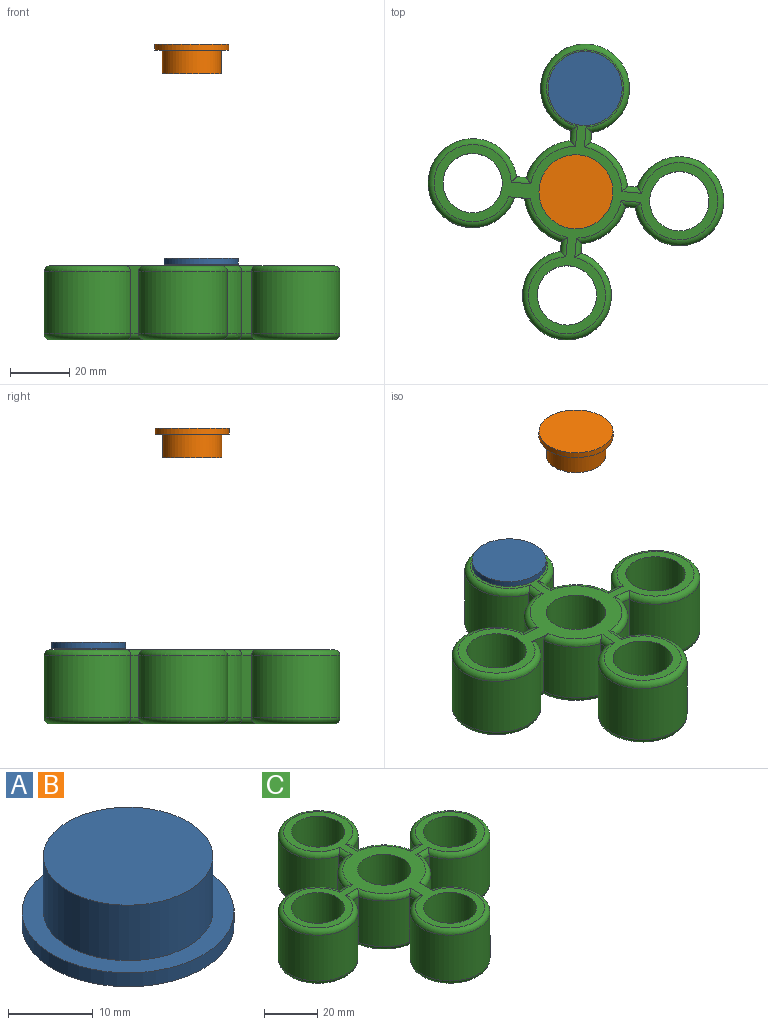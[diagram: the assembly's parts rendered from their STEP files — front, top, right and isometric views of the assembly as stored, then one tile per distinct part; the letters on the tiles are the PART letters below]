
ASSEMBLY  parts=3 mates=2
PART A: 5 faces, bbox 25x25x10 mm
  f0: cylinder r=10mm len=20mm, axis (0,0,-1), area 502.7mm2, adj f1,f3
  f1: plane 20x20mm, normal (0,0,1), area 314.2mm2, adj f0
  f2: cylinder r=12.5mm len=25mm, axis (0,0,-1), area 157.1mm2, adj f3,f4
  f3: plane 25x25mm, normal (0,0,1), area 176.7mm2, adj f0,f2
  f4: plane 25x25mm, normal (0,0,-1), area 490.9mm2, adj f2
PART B: same geometry as A
PART C: 54 faces, bbox 102.6x102.5x25 mm
  f0: plane 21x3.38mm, normal (0,-1,0), area 71.1mm2, adj f1,f19,f32,f38
  f1: cylinder r=17.5mm len=21mm, axis (0,0,-1), area 430mm2, adj f0,f2,f30,f39
  f2: plane 21x3.25mm, normal (-1,0,0), area 68.3mm2, adj f1,f3,f28,f41
  f3: cylinder r=15mm len=30mm, axis (0,0,-1), area 1830.8mm2, adj f2,f4,f26,f43
  f4: plane 23x7.4mm, normal (1,0,0), area 77.3mm2, adj f3,f5,f21,f23,f26,f45
  f5: cylinder r=17.5mm len=21mm, axis (0,0,-1), area 428.5mm2, adj f4,f6,f23,f47
  f6: plane 21x3.23mm, normal (0,-1,0), area 67.9mm2, adj f5,f7,f24,f49
  f7: cylinder r=15mm len=30mm, axis (0,0,-1), area 1830.8mm2, adj f6,f8,f25,f51
  f8: plane 21x3.23mm, normal (0,1,0), area 67.9mm2, adj f7,f9,f27,f53
  f9: cylinder r=17.5mm len=21mm, axis (0,0,-1), area 428.5mm2, adj f8,f10,f29,f52
  f10: plane 21x3.28mm, normal (1,0,0), area 68.9mm2, adj f9,f11,f31,f50
  f11: cylinder r=15mm len=30mm, axis (0,0,-1), area 1829.3mm2, adj f10,f12,f33,f48
  f12: plane 21x3.28mm, normal (-1,0,0), area 68.9mm2, adj f11,f13,f35,f46
  f13: cylinder r=17.5mm len=21mm, axis (0,0,-1), area 428.5mm2, adj f12,f14,f37,f44
  f14: plane 21x3.38mm, normal (0,1,0), area 71.1mm2, adj f13,f19,f36,f42
  f15: cylinder r=10mm len=25mm, axis (0,0,-1), area 1570.8mm2, adj f21,f22
  f16: cylinder r=10mm len=25mm, axis (0,0,-1), area 1570.8mm2, adj f21,f22
  f17: cylinder r=10mm len=25mm, axis (0,0,-1), area 1570.8mm2, adj f21,f22
  f18: cylinder r=10mm len=25mm, axis (0,0,-1), area 1570.8mm2, adj f21,f22
  f19: cylinder r=15mm len=30mm, axis (0,0,-1), area 1830.8mm2, adj f0,f14,f34,f40
  f20: cylinder r=10mm len=25mm, axis (0,0,-1), area 1570.8mm2, adj f21,f22
  f21: plane 96.08x96mm, normal (0,0,1), area 1401mm2, adj f4,f15,f16,f17,f18,f20,f23,f24
  f22: plane 96.08x96mm, normal (0,0,-1), area 1387mm2, adj f15,f16,f17,f18,f20,f38,f39,f40
  f23: torus R=15.5mm, axis (0,0,1), area 62.8mm2, adj f4,f5,f21,f24
  f24: cylinder r=2mm len=6.63mm, axis (-1,0,0), area 13.9mm2, adj f6,f21,f23,f25
  f25: torus R=13mm, axis (0,0,1), area 264.2mm2, adj f7,f21,f24,f27
  f26: torus R=13mm, axis (0,0,1), area 261.9mm2, adj f3,f4,f21,f28
  f27: cylinder r=2mm len=6.63mm, axis (1,0,0), area 13.9mm2, adj f8,f21,f25,f29
  f28: cylinder r=2mm len=6.65mm, axis (0,1,0), area 14mm2, adj f2,f21,f26,f30
  f29: torus R=15.5mm, axis (0,0,1), area 65.1mm2, adj f9,f21,f27,f31
  f30: torus R=15.5mm, axis (0,0,1), area 65.4mm2, adj f1,f21,f28,f32
  f31: cylinder r=2mm len=6.67mm, axis (0,-1,0), area 14.1mm2, adj f10,f21,f29,f33
  f32: cylinder r=2mm len=6.78mm, axis (-1,0,0), area 14.4mm2, adj f0,f21,f30,f34
  f33: torus R=13mm, axis (0,0,1), area 264mm2, adj f11,f21,f31,f35
  f34: torus R=13mm, axis (0,0,1), area 264.2mm2, adj f19,f21,f32,f36
  f35: cylinder r=2mm len=6.67mm, axis (0,1,0), area 14.1mm2, adj f12,f21,f33,f37
  f36: cylinder r=2mm len=6.78mm, axis (1,0,0), area 14.4mm2, adj f14,f21,f34,f37
  f37: torus R=15.5mm, axis (0,0,1), area 65.1mm2, adj f13,f21,f35,f36
  f38: cylinder r=2mm len=6.78mm, axis (1,0,0), area 14.4mm2, adj f0,f22,f39,f40
  f39: torus R=15.5mm, axis (0,0,1), area 65.4mm2, adj f1,f22,f38,f41
  f40: torus R=13mm, axis (0,0,1), area 264.2mm2, adj f19,f22,f38,f42
  f41: cylinder r=2mm len=6.65mm, axis (0,-1,0), area 14mm2, adj f2,f22,f39,f43
  f42: cylinder r=2mm len=6.78mm, axis (-1,0,0), area 14.4mm2, adj f14,f22,f40,f44
  f43: torus R=13mm, axis (0,0,1), area 264.2mm2, adj f3,f22,f41,f45
  f44: torus R=15.5mm, axis (0,0,1), area 65.1mm2, adj f13,f22,f42,f46
  f45: cylinder r=2mm len=6.67mm, axis (0,1,0), area 14.1mm2, adj f4,f22,f43,f47
  f46: cylinder r=2mm len=6.67mm, axis (0,-1,0), area 14.1mm2, adj f12,f22,f44,f48
  f47: torus R=15.5mm, axis (0,0,1), area 65.1mm2, adj f5,f22,f45,f49
  f48: torus R=13mm, axis (0,0,1), area 264mm2, adj f11,f22,f46,f50
  f49: cylinder r=2mm len=6.63mm, axis (1,0,0), area 13.9mm2, adj f6,f22,f47,f51
  f50: cylinder r=2mm len=6.67mm, axis (0,1,0), area 14.1mm2, adj f10,f22,f48,f52
  f51: torus R=13mm, axis (0,0,1), area 264.2mm2, adj f7,f22,f49,f53
  f52: torus R=15.5mm, axis (0,0,1), area 65.1mm2, adj f9,f22,f50,f53
  f53: cylinder r=2mm len=6.63mm, axis (-1,0,0), area 13.9mm2, adj f8,f22,f51,f52
PLACE A rot(axis=(0.04,1,0),180deg) t=(-101.93,13.5,24.92)mm
PLACE B rot(axis=(0.68,-0.74,0),180deg) t=(53.38,-99.43,97.18)mm
PLACE C rot(axis=(0,0,-1),95deg) t=(13.17,18.73,-2.58)mm fixed
MATE slider B.f0 <-> C.f1  axis (0,0,-1) through (13.17,18.73,87.18)mm
MATE slider A.f0 <-> C.f17  axis (0,0,-1) through (16.23,53.71,14.92)mm
